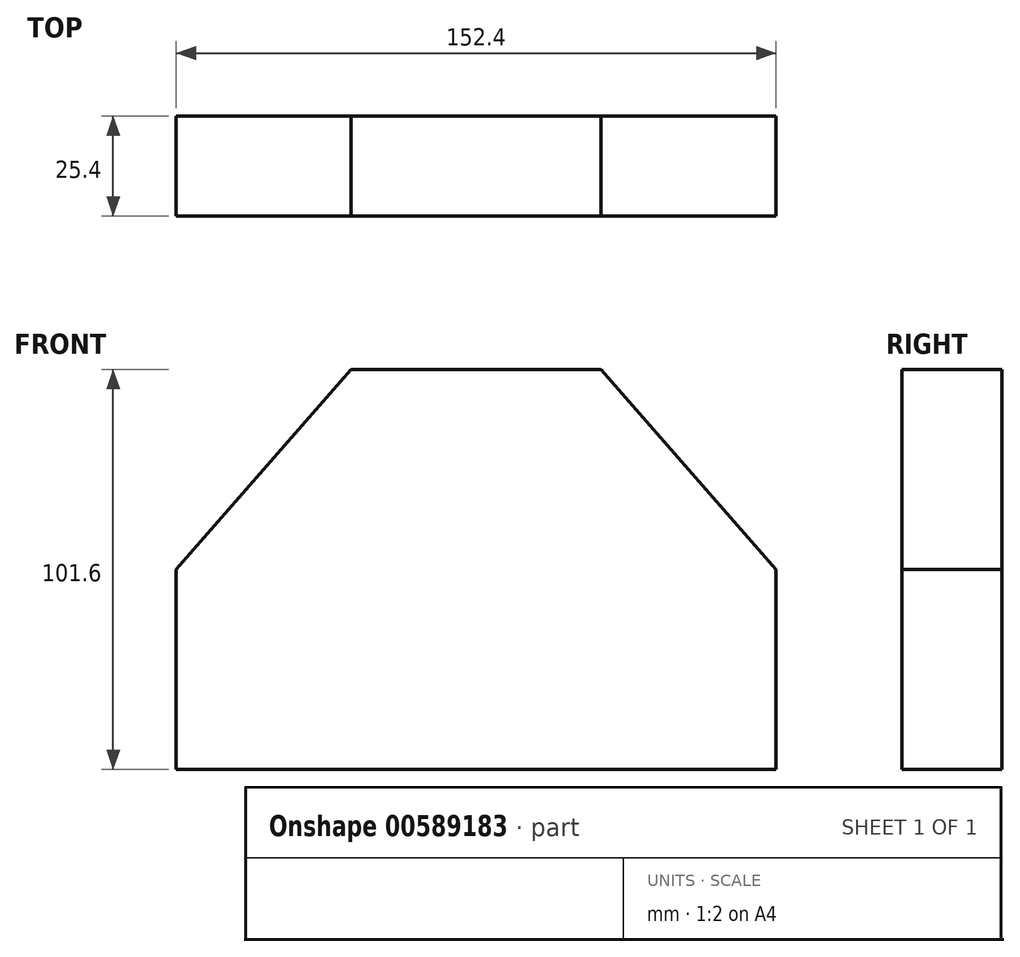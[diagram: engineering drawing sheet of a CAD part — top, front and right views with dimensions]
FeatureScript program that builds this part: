
annotation { "Feature Type Name" : "Feature", "Feature Type Description" : "" }
export const myFeature = defineFeature(function(context is Context, id is Id, definition is map)
    precondition{}
    {
        {
            var Q0;
            Q0=qCreatedBy(makeId("Front.planeOp"),FACE);
            var sketch = newSketch(context, id + "F0", { "sketchPlane" : qUnion([Q0])});
            skLineSegment(sketch, "E0.bottom", {"start": v(76.2, 50.8) * mm, "end": v(-76.2, 50.8) * mm});
            skLineSegment(sketch, "E0.top", {"start": v(76.2, 0) * mm, "end": v(-76.2, 0) * mm});
            skLineSegment(sketch, "E0.left", {"start": v(76.2, 50.8) * mm, "end": v(76.2, 0) * mm});
            skLineSegment(sketch, "E0.right", {"start": v(-76.2, 50.8) * mm, "end": v(-76.2, 0) * mm});
            skPoint(sketch, "E0.middle", {"position": v(0, 101.6) * mm});
            skLineSegment(sketch, "E1", {"start": v(-76.2, 50.8) * mm, "end": v(-31.75, 101.6) * mm});
            skLineSegment(sketch, "E2", {"start": v(-31.75, 101.6) * mm, "end": v(31.75, 101.6) * mm});
            skLineSegment(sketch, "E3", {"start": v(31.75, 101.6) * mm, "end": v(76.2, 50.8) * mm});
            skSolve(sketch);
        }
        {
            var Q0;
            Q0=makeQuery(id+"F0.imprint","IMPRINT",FACE,{"disambiguationData":[TD([[makeQuery(id+"F0.imprint","IMPRINT",EDGE,{"derivedFrom":sQuery(id+"F0.wireOp",EDGE,"E0.bottom")}),-1.0]])]});
            var Q1;
            Q1=makeQuery(id+"F0.imprint","IMPRINT",FACE,{"disambiguationData":[TD([[makeQuery(id+"F0.imprint","IMPRINT",EDGE,{"derivedFrom":sQuery(id+"F0.wireOp",EDGE,"E0.bottom")}),1.0]])]});
            extrude(context, id + "F1", {"entities" : qUnion([Q0, Q1]), "depth" : 25.4 * mm, "offsetDistance" : 25.4 * mm});
        }
    });
